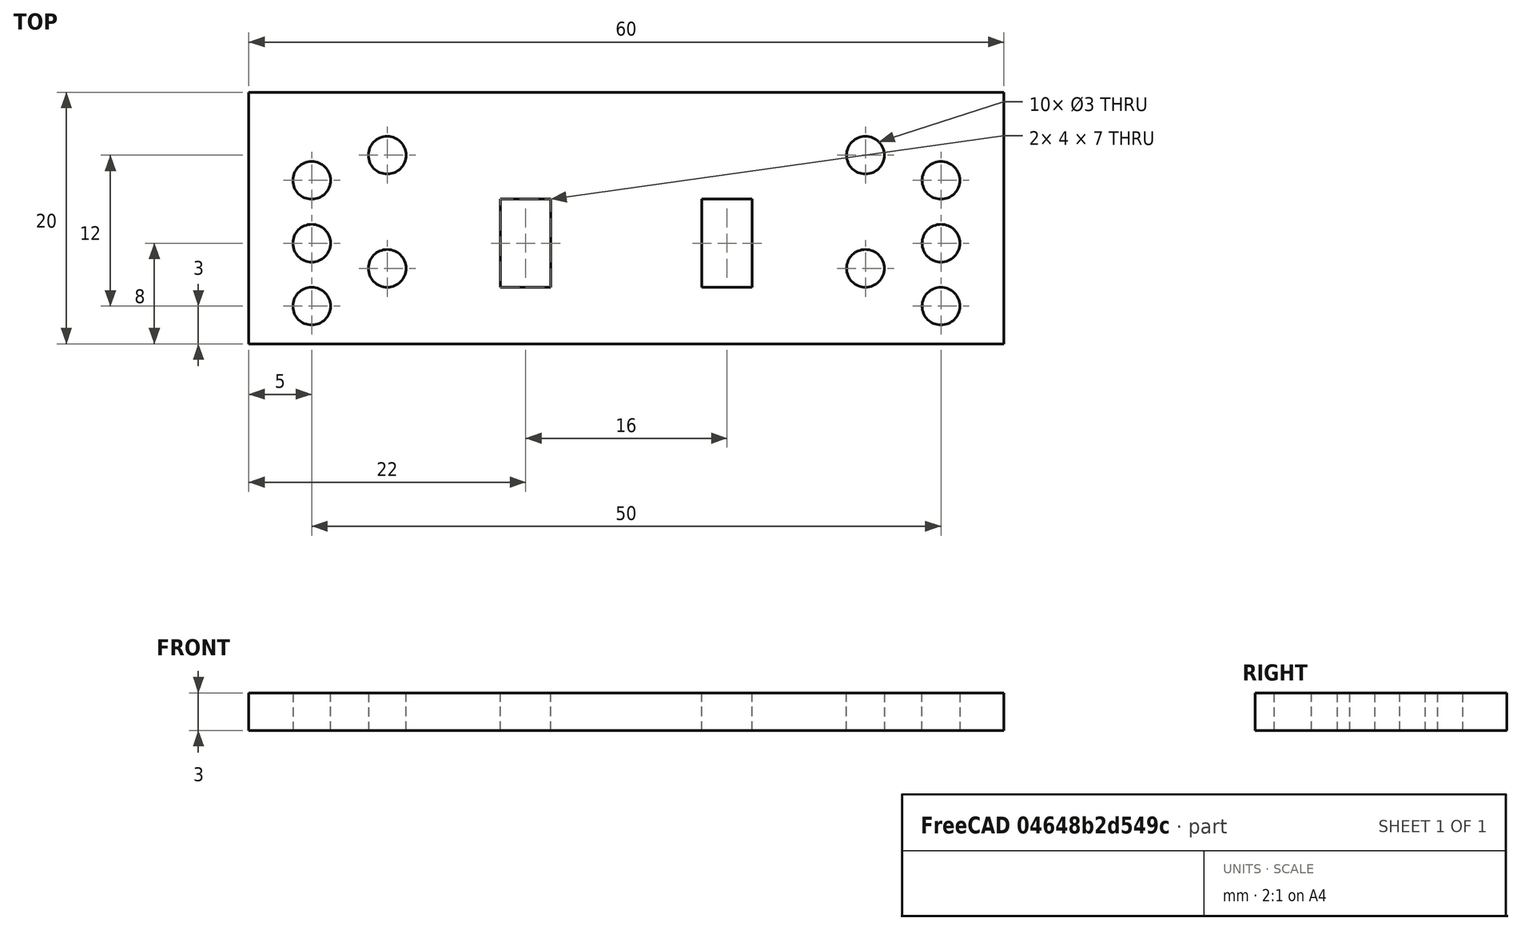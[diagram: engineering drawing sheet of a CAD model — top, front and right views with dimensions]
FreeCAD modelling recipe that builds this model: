
FCSTD DOCUMENT  (FreeCAD 0.16R6707 (Git))
Label: support_guidage_horizontal
License: All rights reserved
LicenseURL: http://en.wikipedia.org/wiki/All_rights_reserved
objects: Sketcher::SketchObject×1, PartDesign::Pad×1, PartDesign::Mirrored×1
note: 4 computed .brp shape members not serialized (recipe doc carries the construction recipe); baked Part::Feature solids carry a one-line shape summary decoded from their .brp

FEATURE [Sketcher::SketchObject] Sketch
  sketch-geometry (20):
    g0: LineSegment StartX=0 StartY=0 StartZ=0 EndX=30 EndY=0 EndZ=0
    g1: LineSegment StartX=30 StartY=0 StartZ=0 EndX=30 EndY=20 EndZ=0
    g2: LineSegment StartX=30 StartY=20 StartZ=0 EndX=0 EndY=20 EndZ=0
    g3: LineSegment StartX=0 StartY=20 StartZ=0 EndX=0 EndY=0 EndZ=0
    g4: GeomPoint [constr] X=5 Y=8 Z=0
    g5: GeomPoint [constr] X=20 Y=8 Z=0
    g6: GeomPoint [constr] X=20 Y=11.5 Z=0
    g7: LineSegment StartX=20 StartY=11.5 StartZ=0 EndX=24 EndY=11.5 EndZ=0
    g8: LineSegment StartX=24 StartY=11.5 StartZ=0 EndX=24 EndY=4.5 EndZ=0
    g9: LineSegment StartX=24 StartY=4.5 StartZ=0 EndX=20 EndY=4.5 EndZ=0
    g10: LineSegment StartX=20 StartY=4.5 StartZ=0 EndX=20 EndY=11.5 EndZ=0
    g11: Circle CenterX=5 CenterY=8 CenterZ=0 NormalX=0 NormalY=0 NormalZ=1 Radius=1.5
    g12: GeomPoint [constr] X=11 Y=6 Z=0
    g13: GeomPoint [constr] X=11 Y=15 Z=0
    g14: Circle CenterX=11 CenterY=15 CenterZ=0 NormalX=0 NormalY=0 NormalZ=1 Radius=1.5
    g15: Circle CenterX=11 CenterY=6 CenterZ=0 NormalX=0 NormalY=0 NormalZ=1 Radius=1.5
    g16: GeomPoint [constr] X=5 Y=13 Z=0
    g17: GeomPoint [constr] X=5 Y=3 Z=0
    g18: Circle CenterX=5 CenterY=13 CenterZ=0 NormalX=0 NormalY=0 NormalZ=1 Radius=1.5
    g19: Circle CenterX=5 CenterY=3 CenterZ=0 NormalX=0 NormalY=0 NormalZ=1 Radius=1.5
  constraints (46):
    c: Coincident(g0,g1)
    c: Coincident(g1,g2)
    c: Coincident(g2,g3)
    c: Coincident(g3,g0)
    c: Horizontal(g0)
    c: Horizontal(g2)
    c: Vertical(g1)
    c: Vertical(g3)
    c: Coincident(g0,g-1)
    c: Distance(g2) = 30
    c: Distance(g3) = 20
    c: DistanceX(g4) = 5
    c: DistanceY(g4) = 8
    c: DistanceY(g5,g4) = 0
    c: DistanceX(g4,g5) = 15
    c: DistanceY(g5,g6) = 3.5
    c: DistanceX(g5,g6) = 0
    c: Coincident(g7,g8)
    c: Coincident(g8,g9)
    c: Coincident(g9,g10)
    c: Coincident(g10,g7)
    c: Horizontal(g7)
    c: Horizontal(g9)
    c: Vertical(g8)
    c: Vertical(g10)
    c: Coincident(g7,g6)
    c: Distance(g7) = 4
    c: Distance(g8) = 7
    c: Coincident(g11,g4)
    c: Radius(g11) = 1.5
    c: DistanceX(g12) = 11
    c: DistanceY(g-1,g12) = 6
    c: DistanceY(g12,g13) = 9
    c: DistanceX(g12,g13) = 0
    c: Coincident(g14,g13)
    c: Coincident(g15,g12)
    c: Radius(g15) = 1.5
    c: Equal(g15,g14)
    c: DistanceY(g17,g4) = 5
    c: DistanceY(g4,g16) = 5
    c: DistanceX(g16,g4) = 0
    c: DistanceX(g17,g4) = 0
    c: Coincident(g18,g16)
    c: Coincident(g19,g17)
    c: Radius(g19) = 1.5
    c: Equal(g19,g18)
FEATURE [PartDesign::Pad] Pad
  Length = 3
  Length2 = 100
  Sketch = -> Sketch
  Type = 0
FEATURE [PartDesign::Mirrored] Mirrored
  MirrorPlane = -> Pad [Face2]
  Originals = -> [Pad]
